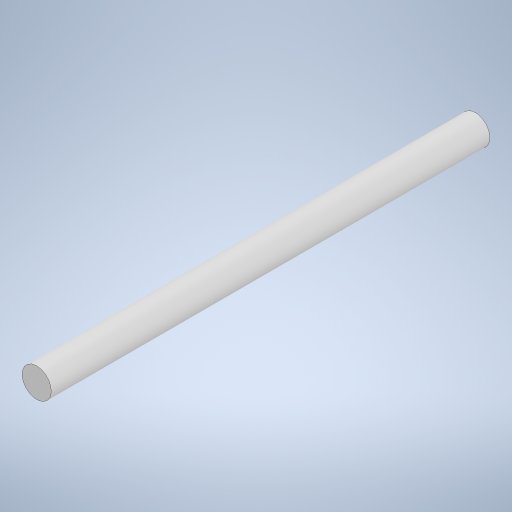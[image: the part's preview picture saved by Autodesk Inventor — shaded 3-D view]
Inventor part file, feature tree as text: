
AUTODESK INVENTOR PART (.ipt)
format: ipt  version: 2023 (Build 270158030, 158C)  size: 256,512 bytes
history: mixed  units: in
note: dims shown in document units (in); Inventor stores cm internally (conversion verified against a paired STEP export)
features: extrude x1, sketch x1, chamfer x1, imported_body x1
ambient origin geometry x8: Origin, YZ Plane, XZ Plane, XY Plane, X Axis, Y Axis, Z Axis, Center Point
bodies: Solid1 (imported_parasolid)
feature tree (4):
  extrude  "Extrusion1"  Depth=0.3937in TaperAngle=0.0deg
  sketch  "Sketch1"  dims[d0=5.9055in d1=0.3937in d2=0.0in]
  chamfer  "Chamfer1"  [1 undecoded]
  imported_body  NMx_Import_Brep_tag  [imported B-rep: ~3 faces, bbox_mm=[0.0, 10.0, 150.0]]
note: 1 required parameter value undecoded (feature->parameter linkage not recoverable at this tier; creation-order binding heuristic only, values carry confidence <= 0.55)
